# Revit family: Bath-Alcove-BubbleMassage-Heated_Surface-KOHLER-Mariposa-K-1224_1
name_source: partatom
category: Plumbing Fixtures
units: mm (PartAtom-declared; Revit-internal decimal feet)

## family parameters
Cut with Voids When Loaded = No
Host = Face
OmniClass Number = 23.31.15.00
OmniClass Title = Bathtubs
Part Type = Normal
Room Calculation Point = No
Round Connector Dimension = Use Diameter
Shared = No

## types (6) — shared parameters
ADA Compliant = No
Amplifer Electrical Connector = Amplifer Electrical Connector
Apparent Load = 1800 VA
Assembly Code = D2010500
Blower Electrical Connector = Blower Electrical Connector
CW Connection = No
Cold Water Inlet = Cold Water Inlet
Date Modified = 03/10/2023
Default Elevation = 0"
Drain Included = Yes
Electrical Connector = Yes
Electrical Note = Two dedicated circuit required, protected with Class A Ground-Fault Circuit-Interrupter (GFCI) or Residual Current Device (RCD)
HW Connection = No
Heater Electrical Connector = Heater Electrical Connector
Height = 21 5/16"
Hot Water Inlet = Hot Water Inlet
Length = 66"
Manufacturer = Kohler Co.
Master Format 2014 = 22 41 19
Master Format 2014 Name = Residential Bathtubs
Material = Acrylic
Product Documentation Link = https://www.us.kohler.com
Product Name = Mariposa
Product Page URL = http://www.us.kohler.com
Pump Electrical Connector = Pump Electrical Connector
URL = https://www.us.kohler.com
Vent Connection = No
Voltage = 120 V
Waste Connection = Yes
Waste Water Outlet = Waste Water Outlet
WaterSense Certified = No
Width = 36"

## per-type parameters (varying)
| type | Description | Finish | Model | Type |
| Left Drain, 0-White | 66 INCH x 36 INCH integral flange Heated BubbleMassage air bath with Bask heated surface and left-hand drain | KOHLER-Acrylic-0-White | K-1224-GHLW-0 | 1 |
| Left Drain, 96-Biscuit | 66 INCH x 36 INCH integral flange Heated BubbleMassage air bath with Bask heated surface and left-hand drain | KOHLER-Acrylic-96-Biscuit | K-1224-GHLW-96 | 2 |
| Left Drain, NY-Dune | 66 INCH x 36 INCH integral flange Heated BubbleMassage air bath with Bask heated surface and left-hand drain | KOHLER-Acrylic-NY-Dune | K-1224-GHLW-NY | 3 |
| Right Drain, 0-White | 66 INCH x 36 INCH integral flange Heated BubbleMassage air bath with Bask heated surface and right-hand drain | KOHLER-Acrylic-0-White | K-1224-GHRW-0 | 4 |
| Right Drain, 96-Biscuit | 66 INCH x 36 INCH integral flange Heated BubbleMassage air bath with Bask heated surface and right-hand drain | KOHLER-Acrylic-96-Biscuit | K-1224-GHRW-96 | 5 |
| Right Drain, NY-Dune | 66 INCH x 36 INCH integral flange Heated BubbleMassage air bath with Bask heated surface and right-hand drain | KOHLER-Acrylic-NY-Dune | K-1224-GHRW-NY | 6 |

## geometry (parser evidence)
native form markers: Sweep x6
no freeform markers — native parametric forms only
